# Revit family: WCSeatCover-Duroplast-SoftClosing-Vitra-MetropoleSeries-122
name_source: partatom
category: Plumbing Fixtures
revit_build: Autodesk Revit 2017 (Build: 20160225_1515(x64)
units: mm (PartAtom-declared; Revit-internal decimal feet)

## family parameters
Cut with Voids When Loaded = No
Host = Face
OmniClass Number = 23.45.05.21.11
OmniClass Title = Water Closets
Part Type = Normal
Room Calculation Point = No
Round Connector Dimension = Use Diameter
Shared = Yes

## types (16) — shared parameters
BIMobject category = Sanitary - Toilet Seats
Brand = VitrA
CW Connection = No
Default Elevation = 410 mm  [stored 1.34514 ft]
Design country = Turkey
HW Connection = No
IFC Classification = Sanitary Terminal
Main Material = Plastic
Manufacturer = VitrA
Manufacturer name = VitrA
Mounting type = Face
NBS Referans Code = 35-93-95
NBS Referans Description = Wc Seats And Covers
Nominal Depth (mm) = 450 mm  [stored 1.47638 ft]
Nominal Height (mm) = 50 mm  [stored 0.164042 ft]
Nominal Width (mm) = 365 mm  [stored 1.19751 ft]
OmniClass Code = 23-31 19 19 11
OmniClass Description = Toilets
Product certification = https://www.vitraglobal.com
UNSPSC Code = 35-93-95
UNSPSC Description = Water Operated Water Closets
URL = https://www.vitraglobal.com
Uniclass 1.4 Code = L72164
Uniclass 1.4 Description = Toilets
Uniclass 2.0 Code = PR-35-93-95
Uniclass 2.0 Description = Wc Seats And Covers
Uniclass 2015 Code = Pr_40_20_93_95
Uniclass 2015 Name = WC seats and covers
Vent Connection = No
Warranty Period (Year) = 2 Years
Waste Connection = No
Weight Net (kg) = 3.5
Youtube = https://www.youtube.com

## per-type parameters (varying)
| type | Article No. (default) | Color | Description | Model | Primary Material | Product SKU | Product data url | Product family | Product group | Product url | Technical description |
| WCSeatCover-Duroplast-SoftClosing-Vitra-122-003-009 | 122-003-009 | White | VitrA WC Seat - Metal Hinge - Top Fixing | 122-003-009 | White | 122-003-009 | https://www.bimobject.com | WC Seat, Metal Hinge, Top Fixing | WC Seat, Metal Hinge, Top Fixing | https://www.vitraglobal.com | https://www.vitraglobal.com |
| WCSeatCover-Duroplast-SoftClosing-QuickRelease-Vitra-MetropoleSeries_122-003R009 | 122-003R009 | White | VitrA Metropole WC Seat - Metal Hinge - Quick Release - Top Fixing | 122-003R009 | White | 122-003R009 |  | Metropole - WC Seat - Metal Hinge - Quick Release - Top Fixing | WC Seat - Metal Hinge - Quick Release - Top Fixing | https://www.vitraglobal.com | https://www.vitraglobal.com |
| WCSeatCover-Duroplast-SoftClosing-Vitra-MetropoleSeries_122-001-009 | 122-001-009 | Matte White | VitrA Metropole WC Seat - Metal Hinge - Top Fixing | 122-001-009 | Matte White | 122-001-009 |  | Metropole - WC Seat - Metal Hinge - Top Fixing | WC Seat - Metal Hinge - Top Fixing | https://www.vitraglobal.com | https://www.vitraglobal.com |
| WCSeatCover-Duroplast-SoftClosing-Quick Release-Vitra-MetropoleSeries_122-001R009 | 122-001R009 | Matte White | VitrA Metropole WC Seat - Metal Hinge -Quick Release -  Top Fixing | 122-001R009 | Matte White | 122-001R009 |  | Metropole - WC Seat - Metal Hinge- Quick Release- Top Fixing | WC Seat - Metal Hinge -Quick Release- Top Fixing | https://www.vitraglobal.com | https://www.vitraglobal.com |
| WCSeatCover-Duroplast-SoftClosing-Vitra-MetropoleSeries_122-020-009 | 122-020-009 | Matte Taupe | VitrA Metropole WC Seat - Metal Hinge - Top Fixing | 122-020-009 | Matte Taupe | 122-020-009 |  | Metropole - WC Seat - Metal Hinge - Top Fixing | WC Seat - Metal Hinge - Top Fixing | https://www.vitraglobal.com | https://www.vitraglobal.com |
| WCSeatCover-Duroplast-SoftClosing-Quick Release-Vitra-MetropoleSeries_122-020R009 | 122-020R009 | Matte Taupe | VitrA Metropole WC Seat - Metal Hinge -Quick Release -  Top Fixing | 122-020R009 | Matte Taupe | 122-020R009 |  | Metropole - WC Seat - Metal Hinge- Quick Release- Top Fixing | WC Seat - Metal Hinge -Quick Release- Top Fixing | https://www.vitraglobal.com | https://www.vitraglobal.com |
| WCSeatCover-Duroplast-SoftClosing-Vitra-MetropoleSeries_122-050-009 | 122-050-009 | Matte Mink | VitrA Metropole WC Seat - Metal Hinge - Top Fixing | 122-050-009 | Matte Mink | 122-050-009 |  | Metropole - WC Seat - Metal Hinge - Top Fixing | WC Seat - Metal Hinge - Top Fixing | https://www.vitraglobal.com | https://www.vitraglobal.com |
| WCSeatCover-Duroplast-SoftClosing-Quick Release-Vitra-MetropoleSeries_122-050R009 | 122-050R009 | Matte Mink | VitrA Metropole WC Seat - Metal Hinge -Quick Release -  Top Fixing | 122-050R009 | Matte Mink | 122-050R009 |  | Metropole - WC Seat - Metal Hinge- Quick Release- Top Fixing | WC Seat - Metal Hinge -Quick Release- Top Fixing | https://www.vitraglobal.com | https://www.vitraglobal.com |
| WCSeatCover-Duroplast-SoftClosing-Vitra-MetropoleSeries_122-070-009 | 122-070-009 | Black | VitrA Metropole WC Seat - Metal Hinge - Top Fixing | 122-070-009 | Black | 122-070-009 |  | Metropole - WC Seat - Metal Hinge - Top Fixing | WC Seat - Metal Hinge - Top Fixing | https://www.vitraglobal.com | https://www.vitraglobal.com |
| WCSeatCover-Duroplast-SoftClosing-Quick Release-Vitra-MetropoleSeries_122-070R009 | 122-070R009 | Black | VitrA Metropole WC Seat - Metal Hinge -Quick Release -  Top Fixing | 122-070R009 | Black | 122-070R009 |  | Metropole - WC Seat - Metal Hinge- Quick Release- Top Fixing | WC Seat - Metal Hinge -Quick Release- Top Fixing | https://www.vitraglobal.com | https://www.vitraglobal.com |
| WCSeatCover-Duroplast-SoftClosing-Vitra-MetropoleSeries_122-083-009 | 122-083-009 | Matte Black | VitrA Metropole WC Seat - Metal Hinge - Top Fixing | 122-083-009 | Matte Black | 122-083-009 |  | Metropole - WC Seat - Metal Hinge - Top Fixing | WC Seat - Metal Hinge - Top Fixing | https://www.vitraglobal.com | https://www.vitraglobal.com |
| WCSeatCover-Duroplast-SoftClosing-Quick Release-Vitra-MetropoleSeries_122-083R009 | 122-083R009 | Matte Black | VitrA Metropole WC Seat - Metal Hinge -Quick Release -  Top Fixing | 122-083R009 | Matte Black | 122-083R009 |  | Metropole - WC Seat - Metal Hinge- Quick Release- Top Fixing | WC Seat - Metal Hinge -Quick Release- Top Fixing | https://www.vitraglobal.com | https://www.vitraglobal.com |
| WCSeatCover-Duroplast-SoftClosing-QuickRelease-Vitra-MetropoleSeries_122-003H209 | 122-003H209 | White | VitrA Metropole WC Seat - Metal Hinge - Quick Release - Top Fixing | 122-003H209 | White | 122-003H209 |  | Metropole - WC Seat - Metal Hinge - Quick Release - Top Fixing | WC Seat - Metal Hinge - Quick Release - Top Fixing | https://www.vitra-india.com | https://www.vitra-india.com |
| WCSeatCover-Duroplast-SoftClosing-Quick Release-Vitra-MetropoleSeries_122-020H209 | 122-020H209 | Matte Taupe | VitrA Metropole WC Seat - Metal Hinge -Quick Release -  Top Fixing | 122-020H209 | Matte Taupe | 122-020H209 |  | Metropole - WC Seat - Metal Hinge- Quick Release- Top Fixing | WC Seat - Metal Hinge -Quick Release- Top Fixing | https://www.vitra-india.com | https://www.vitra-india.com |
| WCSeatCover-Duroplast-SoftClosing-Quick Release-Vitra-MetropoleSeries_122-050H209 | 122-050H209 | Matte Mink | VitrA Metropole WC Seat - Metal Hinge -Quick Release -  Top Fixing | 122-050H209 | Matte Mink | 122-050H209 |  | Metropole - WC Seat - Metal Hinge- Quick Release- Top Fixing | WC Seat - Metal Hinge -Quick Release- Top Fixing | https://www.vitra-india.com | https://www.vitra-india.com |
| WCSeatCover-Duroplast-SoftClosing-Quick Release-Vitra-MetropoleSeries_122-083H209 | 122-083H209 | Matte Black | VitrA Metropole WC Seat - Metal Hinge -Quick Release -  Top Fixing | 122-083H209 | Matte Black | 122-083H209 |  | Metropole - WC Seat - Metal Hinge- Quick Release- Top Fixing | WC Seat - Metal Hinge -Quick Release- Top Fixing | https://www.vitra-india.com | https://www.vitra-india.com |

note: [stored X ft] marks values corroborated as IEEE doubles in the binary element streams (Revit-internal decimal feet)

## geometry (parser evidence)
native form markers: Sweep x2
no freeform markers — native parametric forms only
